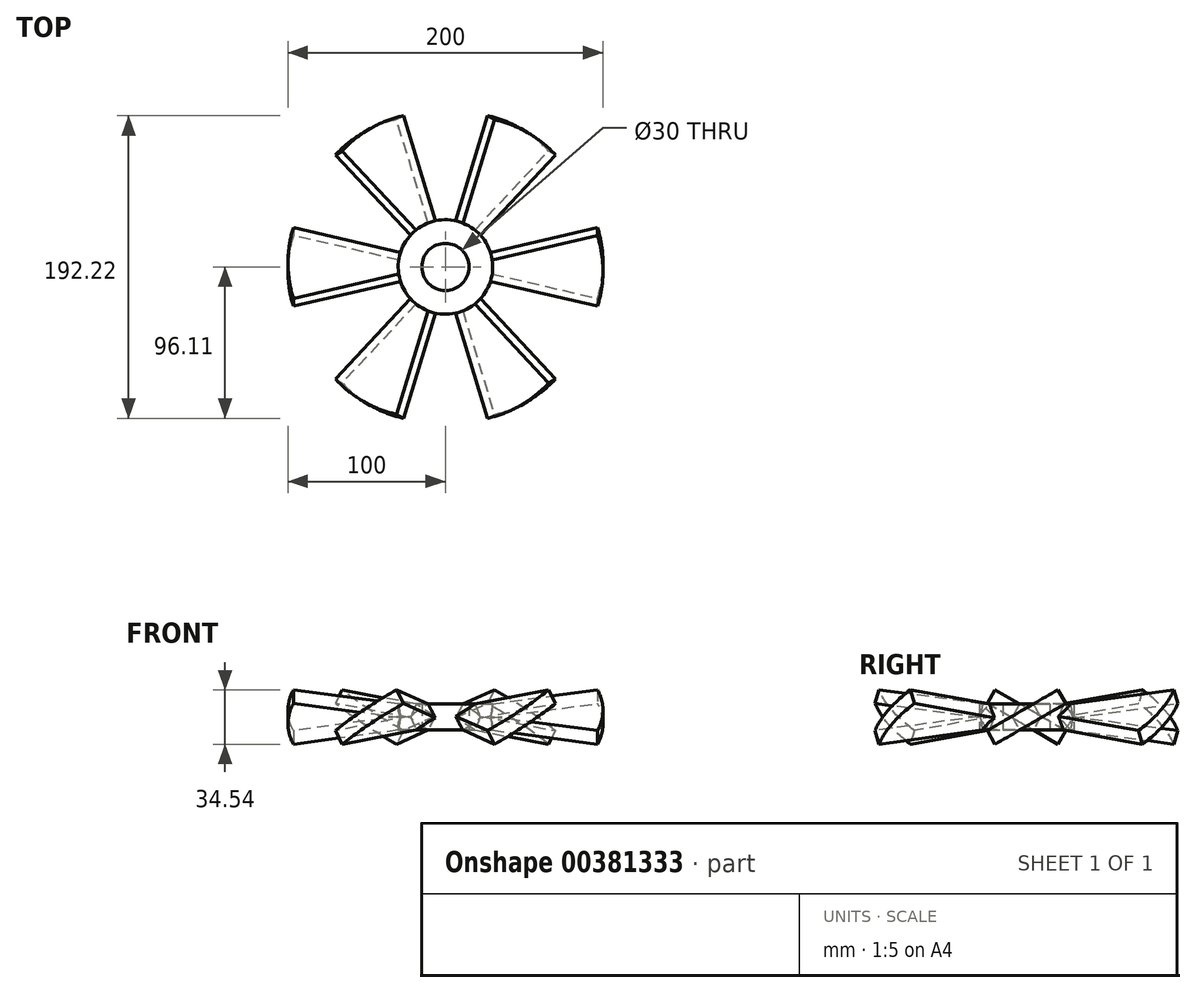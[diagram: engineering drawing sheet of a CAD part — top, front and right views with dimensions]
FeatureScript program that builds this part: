
annotation { "Feature Type Name" : "Feature", "Feature Type Description" : "" }
export const myFeature = defineFeature(function(context is Context, id is Id, definition is map)
    precondition{}
    {
        {
            var Q0;
            Q0=qCreatedBy(makeId("Top.planeOp"),FACE);
            var sketch = newSketch(context, id + "F0", { "sketchPlane" : qUnion([Q0])});
            skArc(sketch, "E0", {"start": v(96.6, 25.88) * mm, "mid": v(100, 0) * mm, "end": v(96.6, -25.88) * mm});
            skLineSegment(sketch, "E1", {"start": v(0, 0) * mm, "end": v(96.6, -25.88) * mm});
            skLineSegment(sketch, "E2.MirrorCS", {"start": v(0, 0) * mm, "end": v(96.6, 25.88) * mm});
            skSolve(sketch);
        }
        {
            var Q0;
            Q0=qCreatedBy(makeId("Top.planeOp"),FACE);
            var sketch = newSketch(context, id + "F1", { "sketchPlane" : qUnion([Q0])});
            skLineSegment(sketch, "E3", {"start": v(0, 0) * mm, "end": v(116.94, 0) * mm, "construction": true});
            skSolve(sketch);
        }
        {
            var Q0;
            Q0 = qSketchRegion(id + "F0", true);
            extrude(context, id + "F2", {"entities" : qUnion([Q0]), "endBound" : BoundingType.SYMMETRIC, "depth" : 10 * mm});
        }
        {
            var Q0;
            Q0=makeQuery(id+"F2.opExtrude","SWEPT_BODY",BODY,{"disambiguationData":[OSD([sQuery(id+"F0.wireOp",EDGE,"E0"),sQuery(id+"F0.wireOp",EDGE,"E1"),sQuery(id+"F0.wireOp",EDGE,"E2.MirrorCS")])]});
            var Q1;
            Q1=sQuery(id+"F1.wireOp",EDGE,"E3");
            transform(context, id + "F3", {"entities" : qUnion([Q0]), "transformType" : TransformType.ROTATION, "transformAxis" : qUnion([Q1]), "angle" : 30 * degree, "makeCopy" : false});
        }
        {
            var Q0;
            Q0=qCreatedBy(makeId("Front.planeOp"),FACE);
            var sketch = newSketch(context, id + "F4", { "sketchPlane" : qUnion([Q0])});
            skLineSegment(sketch, "E4", {"start": v(0, 0) * mm, "end": v(0, 41.2) * mm, "construction": true});
            skSolve(sketch);
        }
        {
            var Q0;
            Q0=makeQuery(id+"F2.opExtrude","SWEPT_BODY",BODY,{"disambiguationData":[OSD([sQuery(id+"F0.wireOp",EDGE,"E0"),sQuery(id+"F0.wireOp",EDGE,"E1"),sQuery(id+"F0.wireOp",EDGE,"E2.MirrorCS")])]});
            var Q1;
            Q1=sQuery(id+"F4.wireOp",EDGE,"E4");
            circularPattern(context, id + "F5", {"entities" : qUnion([Q0]), "axis" : qUnion([Q1]), "angle" : 360 * degree, "instanceCount" : 6, "equalSpace" : true});
        }
        {
            var Q0;
            Q0=qCreatedBy(makeId("Top.planeOp"),FACE);
            var sketch = newSketch(context, id + "F6", { "sketchPlane" : qUnion([Q0])});
            skCircle(sketch, "E5", {"center": v(0, 0) * mm, "radius": 30 * mm});
            skSolve(sketch);
        }
        {
            var Q0;
            Q0 = qSketchRegion(id + "F6", true);
            extrude(context, id + "F7", {"entities" : qUnion([Q0]), "endBound" : BoundingType.SYMMETRIC, "depth" : 25 * mm});
        }
        {
            var Q0;
            Q0=makeQuery(id+"F5.opPattern","COPY",BODY,{"derivedFrom":makeQuery(id+"F2.opExtrude","SWEPT_BODY",BODY,{"disambiguationData":[OSD([sQuery(id+"F0.wireOp",EDGE,"E0"),sQuery(id+"F0.wireOp",EDGE,"E1"),sQuery(id+"F0.wireOp",EDGE,"E2.MirrorCS")])]}),"instanceName":"5"});
            var Q1;
            Q1=makeQuery(id+"F7.opExtrude","SWEPT_BODY",BODY,{"disambiguationData":[OSD([sQuery(id+"F6.wireOp",EDGE,"E5")])]});
            var Q2;
            Q2=makeQuery(id+"F5.opPattern","COPY",BODY,{"derivedFrom":makeQuery(id+"F2.opExtrude","SWEPT_BODY",BODY,{"disambiguationData":[OSD([sQuery(id+"F0.wireOp",EDGE,"E0"),sQuery(id+"F0.wireOp",EDGE,"E1"),sQuery(id+"F0.wireOp",EDGE,"E2.MirrorCS")])]}),"instanceName":"2"});
            var Q3;
            Q3=makeQuery(id+"F5.opPattern","COPY",BODY,{"derivedFrom":makeQuery(id+"F2.opExtrude","SWEPT_BODY",BODY,{"disambiguationData":[OSD([sQuery(id+"F0.wireOp",EDGE,"E0"),sQuery(id+"F0.wireOp",EDGE,"E1"),sQuery(id+"F0.wireOp",EDGE,"E2.MirrorCS")])]}),"instanceName":"4"});
            var Q4;
            Q4=makeQuery(id+"F5.opPattern","COPY",BODY,{"derivedFrom":makeQuery(id+"F2.opExtrude","SWEPT_BODY",BODY,{"disambiguationData":[OSD([sQuery(id+"F0.wireOp",EDGE,"E0"),sQuery(id+"F0.wireOp",EDGE,"E1"),sQuery(id+"F0.wireOp",EDGE,"E2.MirrorCS")])]}),"instanceName":"1"});
            var Q5;
            Q5=makeQuery(id+"F5.opPattern","COPY",BODY,{"derivedFrom":makeQuery(id+"F2.opExtrude","SWEPT_BODY",BODY,{"disambiguationData":[OSD([sQuery(id+"F0.wireOp",EDGE,"E0"),sQuery(id+"F0.wireOp",EDGE,"E1"),sQuery(id+"F0.wireOp",EDGE,"E2.MirrorCS")])]}),"instanceName":"3"});
            var Q6;
            Q6=makeQuery(id+"F2.opExtrude","SWEPT_BODY",BODY,{"disambiguationData":[OSD([sQuery(id+"F0.wireOp",EDGE,"E0"),sQuery(id+"F0.wireOp",EDGE,"E1"),sQuery(id+"F0.wireOp",EDGE,"E2.MirrorCS")])]});
            booleanBodies(context, id + "F8", {"operationType" : BooleanOperationType.UNION, "tools" : qUnion([Q0, Q1, Q2, Q3, Q4, Q5, Q6])});
        }
        {
            var Q0;
            {var subQ0=sQuery(id+"F0.wireOp",EDGE,"E2.MirrorCS");Q0=makeQuery(id+"F8.opBoolean","INTERSECT",VERTEX,{"derivedFrom":[makeQuery(id+"F5.opPattern","COPY",FACE,{"derivedFrom":makeQuery(id+"F2.opExtrude","CAP_FACE",FACE,{"disambiguationData":[OSD([sQuery(id+"F0.wireOp",EDGE,"E0"),sQuery(id+"F0.wireOp",EDGE,"E1"),subQ0])],"isStart":false}),"instanceName":"5"}),makeQuery(id+"F5.opPattern","COPY",FACE,{"derivedFrom":makeQuery(id+"F2.opExtrude","SWEPT_FACE",FACE,{"disambiguationData":[OSD([subQ0])]}),"instanceName":"5"}),makeQuery(id+"F7.opExtrude","SWEPT_FACE",FACE,{"disambiguationData":[OSD([sQuery(id+"F6.wireOp",EDGE,"E5")])]})]});}
            var Q1;
            {var subQ0=sQuery(id+"F0.wireOp",EDGE,"E2.MirrorCS");Q1=makeQuery(id+"F8.opBoolean","INTERSECT",VERTEX,{"derivedFrom":[makeQuery(id+"F5.opPattern","COPY",FACE,{"derivedFrom":makeQuery(id+"F2.opExtrude","CAP_FACE",FACE,{"disambiguationData":[OSD([sQuery(id+"F0.wireOp",EDGE,"E0"),sQuery(id+"F0.wireOp",EDGE,"E1"),subQ0])],"isStart":false}),"instanceName":"1"}),makeQuery(id+"F5.opPattern","COPY",FACE,{"derivedFrom":makeQuery(id+"F2.opExtrude","SWEPT_FACE",FACE,{"disambiguationData":[OSD([subQ0])]}),"instanceName":"1"}),makeQuery(id+"F7.opExtrude","SWEPT_FACE",FACE,{"disambiguationData":[OSD([sQuery(id+"F6.wireOp",EDGE,"E5")])]})]});}
            var Q2;
            {var subQ0=sQuery(id+"F0.wireOp",EDGE,"E2.MirrorCS");Q2=makeQuery(id+"F8.opBoolean","INTERSECT",VERTEX,{"derivedFrom":[makeQuery(id+"F5.opPattern","COPY",FACE,{"derivedFrom":makeQuery(id+"F2.opExtrude","CAP_FACE",FACE,{"disambiguationData":[OSD([sQuery(id+"F0.wireOp",EDGE,"E0"),sQuery(id+"F0.wireOp",EDGE,"E1"),subQ0])],"isStart":false}),"instanceName":"3"}),makeQuery(id+"F5.opPattern","COPY",FACE,{"derivedFrom":makeQuery(id+"F2.opExtrude","SWEPT_FACE",FACE,{"disambiguationData":[OSD([subQ0])]}),"instanceName":"3"}),makeQuery(id+"F7.opExtrude","SWEPT_FACE",FACE,{"disambiguationData":[OSD([sQuery(id+"F6.wireOp",EDGE,"E5")])]})]});}
            cPlane(context, id + "F9", {"entities" : qUnion([Q0, Q1, Q2]), "cplaneType" : CPlaneType.THREE_POINT, "offset" : 25 * mm, "width" : 150 * mm, "height" : 150 * mm});
        }
        {
            var Q0;
            Q0=makeQuery(id+"F7.opExtrude","CAP_FACE",FACE,{"disambiguationData":[OSD([sQuery(id+"F6.wireOp",EDGE,"E5")])],"isStart":false});
            var Q1;
            Q1=qCreatedBy(id+"F9.planeOp",FACE);
            extrude(context, id + "F10", {"entities" : qUnion([Q0]), "operationType" : NewBodyOperationType.REMOVE, "endBound" : BoundingType.UP_TO_SURFACE, "oppositeDirection" : true, "endBoundEntityFace" : qUnion([Q1]), "depth" : 25 * mm});
        }
        {
            var Q0;
            {var subQ0=sQuery(id+"F0.wireOp",EDGE,"E1");Q0=makeQuery(id+"F8.opBoolean","INTERSECT",VERTEX,{"derivedFrom":[makeQuery(id+"F5.opPattern","COPY",FACE,{"derivedFrom":makeQuery(id+"F2.opExtrude","CAP_FACE",FACE,{"disambiguationData":[OSD([sQuery(id+"F0.wireOp",EDGE,"E0"),subQ0,sQuery(id+"F0.wireOp",EDGE,"E2.MirrorCS")])],"isStart":true}),"instanceName":"4"}),makeQuery(id+"F5.opPattern","COPY",FACE,{"derivedFrom":makeQuery(id+"F2.opExtrude","SWEPT_FACE",FACE,{"disambiguationData":[OSD([subQ0])]}),"instanceName":"4"}),makeQuery(id+"F7.opExtrude","SWEPT_FACE",FACE,{"disambiguationData":[OSD([sQuery(id+"F6.wireOp",EDGE,"E5")])]})]});}
            var Q1;
            {var subQ0=sQuery(id+"F0.wireOp",EDGE,"E1");Q1=makeQuery(id+"F8.opBoolean","INTERSECT",VERTEX,{"derivedFrom":[makeQuery(id+"F5.opPattern","COPY",FACE,{"derivedFrom":makeQuery(id+"F2.opExtrude","CAP_FACE",FACE,{"disambiguationData":[OSD([sQuery(id+"F0.wireOp",EDGE,"E0"),subQ0,sQuery(id+"F0.wireOp",EDGE,"E2.MirrorCS")])],"isStart":true}),"instanceName":"2"}),makeQuery(id+"F5.opPattern","COPY",FACE,{"derivedFrom":makeQuery(id+"F2.opExtrude","SWEPT_FACE",FACE,{"disambiguationData":[OSD([subQ0])]}),"instanceName":"2"}),makeQuery(id+"F7.opExtrude","SWEPT_FACE",FACE,{"disambiguationData":[OSD([sQuery(id+"F6.wireOp",EDGE,"E5")])]})]});}
            var Q2;
            {var subQ0=sQuery(id+"F0.wireOp",EDGE,"E1");Q2=makeQuery(id+"F8.opBoolean","INTERSECT",VERTEX,{"derivedFrom":[makeQuery(id+"F2.opExtrude","CAP_FACE",FACE,{"disambiguationData":[OSD([sQuery(id+"F0.wireOp",EDGE,"E0"),subQ0,sQuery(id+"F0.wireOp",EDGE,"E2.MirrorCS")])],"isStart":true}),makeQuery(id+"F2.opExtrude","SWEPT_FACE",FACE,{"disambiguationData":[OSD([subQ0])]}),makeQuery(id+"F7.opExtrude","SWEPT_FACE",FACE,{"disambiguationData":[OSD([sQuery(id+"F6.wireOp",EDGE,"E5")])]})]});}
            cPlane(context, id + "F11", {"entities" : qUnion([Q0, Q1, Q2]), "cplaneType" : CPlaneType.THREE_POINT, "offset" : 25 * mm, "width" : 150 * mm, "height" : 150 * mm});
        }
        {
            var Q0;
            Q0=makeQuery(id+"F7.opExtrude","CAP_FACE",FACE,{"disambiguationData":[OSD([sQuery(id+"F6.wireOp",EDGE,"E5")])],"isStart":true});
            var Q1;
            Q1=qCreatedBy(id+"F11.planeOp",FACE);
            extrude(context, id + "F12", {"entities" : qUnion([Q0]), "operationType" : NewBodyOperationType.REMOVE, "endBound" : BoundingType.UP_TO_SURFACE, "oppositeDirection" : true, "endBoundEntityFace" : qUnion([Q1]), "depth" : 25 * mm});
        }
        {
            var Q0;
            Q0=makeQuery(id+"F12.boolean.opBoolean","COPY",FACE,{"derivedFrom":makeQuery(id+"F12.opExtrude","CAP_FACE",FACE,{"disambiguationData":[OSD([sQuery(id+"F6.wireOp",EDGE,"E5")])],"isStart":false})});
            var sketch = newSketch(context, id + "F13", { "sketchPlane" : qUnion([Q0])});
            skCircle(sketch, "E6", {"center": v(0, 0) * mm, "radius": 15 * mm});
            skSolve(sketch);
        }
        {
            var Q0;
            Q0=makeQuery(id+"F13.imprint","IMPRINT",FACE,{"disambiguationData":[TD([[makeQuery(id+"F13.imprint","IMPRINT",EDGE,{"derivedFrom":sQuery(id+"F13.wireOp",EDGE,"E6")}),1.0]])]});
            extrude(context, id + "F14", {"entities" : qUnion([Q0]), "operationType" : NewBodyOperationType.REMOVE, "endBound" : BoundingType.UP_TO_NEXT, "oppositeDirection" : true, "depth" : 25 * mm});
        }
    });
